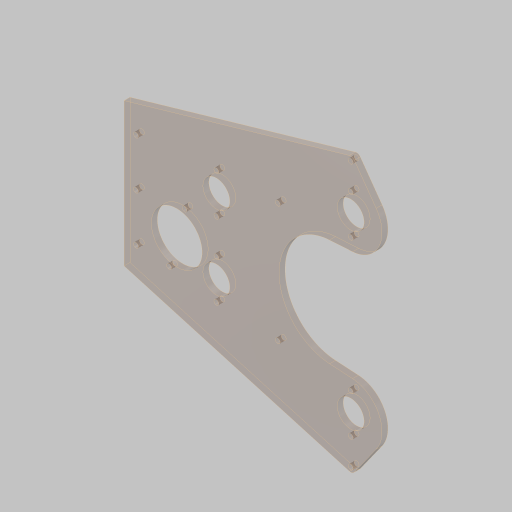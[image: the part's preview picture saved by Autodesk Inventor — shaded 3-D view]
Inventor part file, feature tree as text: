
AUTODESK INVENTOR PART (.ipt)
format: ipt  version: 2023.5 (Build 275446000, 446)  size: 193,024 bytes
history: native  units: in
note: dims shown in document units (in); Inventor stores cm internally (conversion verified against a paired STEP export)
features: sketch x1, extrude x1, hole x1
ambient origin geometry x8: Origin, YZ Plane, XZ Plane, XY Plane, X Axis, Y Axis, Z Axis, Center Point
bodies: Solid1 (feature_tree)
feature tree (3):
  sketch  "Sketch1"  dims[d0=3.0in d1=3.0in d2=4.5in d4=7.2284in d5=1.125in d6=0.75in d7=1.128in d8=1.88in d9=3.125in d10=5.6298in d11=5.992in d12=1.125in d13=0.4688in d14=0.75in d15=1.375in d16=2.3622in d18=360.0deg d20=0.25in d21=2.125in d22=1.0in d23=6.0in d24=9.5in d26=5.0in d27=0.25in d28=0.0in d29=0.375in d30=0.25in d32=1.655in d33=1.655in d34=1.655in d35=1.655in d36=1.0in d37=0.201in d38=0.75in d39=0.385in d40=0.25in d41=0.5635in d42=1.0in d43=0.8108in d44=4.0in d45=2.125in d46=2.5in d47=15.0deg]
  extrude  "Extrusion1"  Depth=0.25in
  hole  "Hole1"  [1 undecoded]
note: 1 required parameter value undecoded (feature->parameter linkage not recoverable at this tier; creation-order binding heuristic only, values carry confidence <= 0.55)
